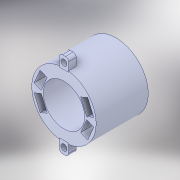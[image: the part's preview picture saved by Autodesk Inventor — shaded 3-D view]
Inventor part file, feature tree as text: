
AUTODESK INVENTOR PART (.ipt)
format: ipt  version: 2018.2 (Build 222227000, 227)  size: 175,104 bytes
history: native  units: in
note: dims shown in document units (in); Inventor stores cm internally (conversion verified against a paired STEP export)
features: fillet x1
ambient origin geometry x8: Origin, YZ Plane, XZ Plane, XY Plane, X Axis, Y Axis, Z Axis, Center Point
bodies: Solid1 (feature_tree)
feature tree (1):
  fillet  "Fillet2"  [1 undecoded]
note: 1 required parameter value undecoded (feature->parameter linkage not recoverable at this tier; creation-order binding heuristic only, values carry confidence <= 0.55)
